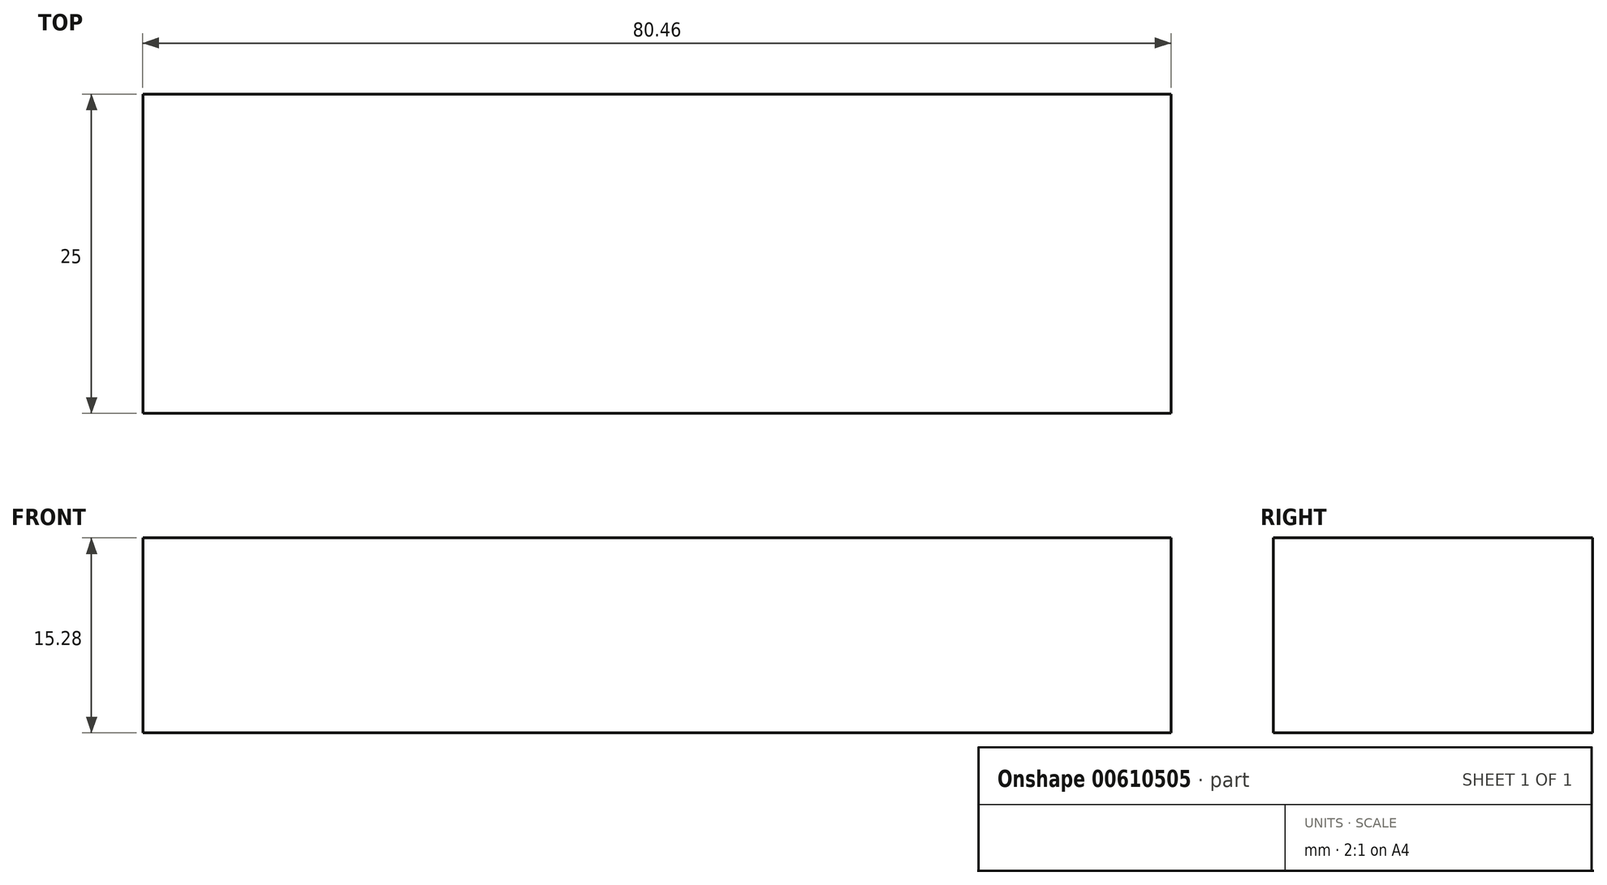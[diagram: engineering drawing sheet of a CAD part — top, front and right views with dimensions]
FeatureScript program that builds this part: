
annotation { "Feature Type Name" : "Feature", "Feature Type Description" : "" }
export const myFeature = defineFeature(function(context is Context, id is Id, definition is map)
    precondition{}
    {
        {
            var Q0;
            Q0=qCreatedBy(makeId("Front.planeOp"),FACE);
            var sketch = newSketch(context, id + "F0", { "sketchPlane" : qUnion([Q0])});
            skLineSegment(sketch, "E0.bottom", {"start": v(40.23, -7.64) * mm, "end": v(-40.23, -7.64) * mm});
            skLineSegment(sketch, "E0.top", {"start": v(40.23, 7.64) * mm, "end": v(-40.23, 7.64) * mm});
            skLineSegment(sketch, "E0.left", {"start": v(40.23, -7.64) * mm, "end": v(40.23, 7.64) * mm});
            skLineSegment(sketch, "E0.right", {"start": v(-40.23, -7.64) * mm, "end": v(-40.23, 7.64) * mm});
            skPoint(sketch, "E0.middle", {"position": v(0, 0) * mm});
            skSolve(sketch);
        }
        {
            var Q0;
            Q0 = qSketchRegion(id + "F0", true);
            extrude(context, id + "F1", {"entities" : qUnion([Q0]), "endBound" : BoundingType.SYMMETRIC, "depth" : 25 * mm, "offsetDistance" : 25 * mm});
        }
    });
